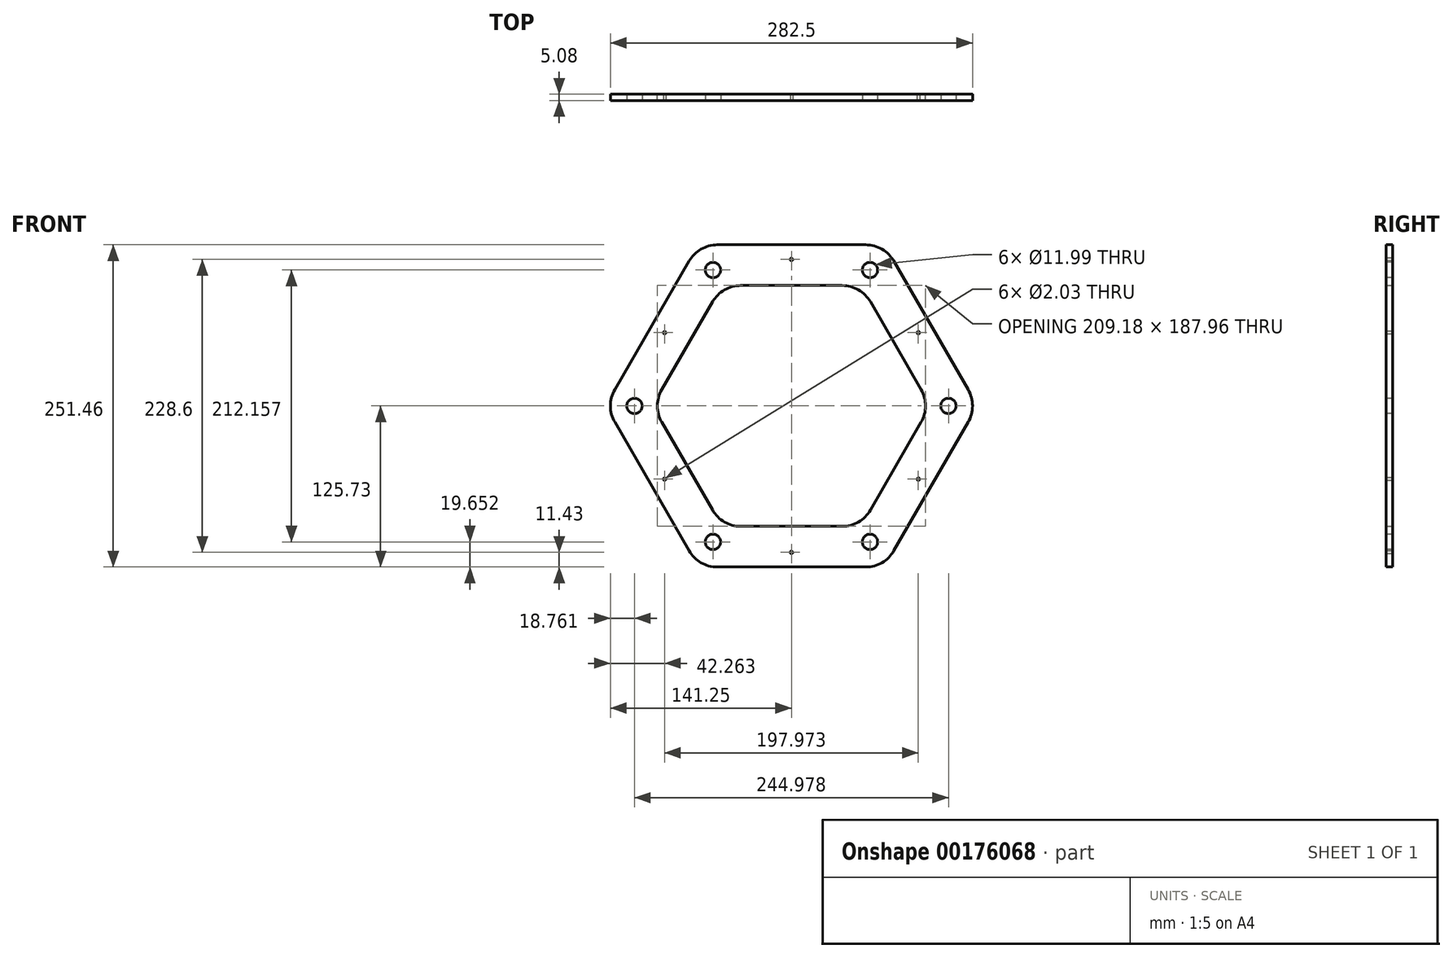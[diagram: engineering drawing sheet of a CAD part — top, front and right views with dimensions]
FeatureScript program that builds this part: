
annotation { "Feature Type Name" : "Feature", "Feature Type Description" : "" }
export const myFeature = defineFeature(function(context is Context, id is Id, definition is map)
    precondition{}
    {
        {
            var Q0;
            Q0=qCreatedBy(makeId("Front.planeOp"),FACE);
            var sketch = newSketch(context, id + "F0", { "sketchPlane" : qUnion([Q0])});
            skCircle(sketch, "E0.cCircle", {"center": v(0, 0) * mm, "radius": 93.98 * mm, "construction": true});
            skLineSegment(sketch, "E0.0", {"start": v(61.6, 81.28) * mm, "end": v(101.19, 12.7) * mm});
            skLineSegment(sketch, "E0.1", {"start": v(101.19, -12.7) * mm, "end": v(61.6, -81.28) * mm});
            skLineSegment(sketch, "E0.2", {"start": v(39.6, -93.98) * mm, "end": v(-39.6, -93.98) * mm});
            skLineSegment(sketch, "E0.3", {"start": v(-61.6, -81.28) * mm, "end": v(-101.19, -12.7) * mm});
            skLineSegment(sketch, "E0.4", {"start": v(-101.19, 12.7) * mm, "end": v(-61.6, 81.28) * mm});
            skLineSegment(sketch, "E0.5", {"start": v(-39.6, 93.98) * mm, "end": v(39.6, 93.98) * mm});
            skPoint(sketch, "E0.0.midPoint", {"position": v(81.39, 46.99) * mm});
            skCircle(sketch, "E1.cCircle", {"center": v(0, 0) * mm, "radius": 125.73 * mm, "construction": true});
            skLineSegment(sketch, "E1.0", {"start": v(-57.93, 125.73) * mm, "end": v(57.93, 125.73) * mm});
            skLineSegment(sketch, "E1.1", {"start": v(79.92, 113.03) * mm, "end": v(137.85, 12.7) * mm});
            skLineSegment(sketch, "E1.2", {"start": v(137.85, -12.7) * mm, "end": v(79.92, -113.03) * mm});
            skLineSegment(sketch, "E1.3", {"start": v(57.93, -125.73) * mm, "end": v(-57.93, -125.73) * mm});
            skLineSegment(sketch, "E1.4", {"start": v(-79.92, -113.03) * mm, "end": v(-137.85, -12.7) * mm});
            skLineSegment(sketch, "E1.5", {"start": v(-137.85, 12.7) * mm, "end": v(-79.92, 113.03) * mm});
            skPoint(sketch, "E1.0.midPoint", {"position": v(0, 125.73) * mm});
            skPoint(sketch, "E2.visualSharp", {"position": v(-72.6, 125.73) * mm});
            skArc(sketch, "E2.filletArc", {"start": v(-57.93, 125.73) * mm, "mid": v(-70.63, 122.33) * mm, "end": v(-79.92, 113.03) * mm});
            skPoint(sketch, "E3.visualSharp", {"position": v(72.6, 125.73) * mm});
            skArc(sketch, "E3.filletArc", {"start": v(79.92, 113.03) * mm, "mid": v(70.63, 122.33) * mm, "end": v(57.93, 125.73) * mm});
            skPoint(sketch, "E4.visualSharp", {"position": v(145.18, 0) * mm});
            skArc(sketch, "E4.filletArc", {"start": v(137.85, -12.7) * mm, "mid": v(141.25, 0) * mm, "end": v(137.85, 12.7) * mm});
            skPoint(sketch, "E5.visualSharp", {"position": v(72.6, -125.73) * mm});
            skArc(sketch, "E5.filletArc", {"start": v(57.93, -125.73) * mm, "mid": v(70.63, -122.33) * mm, "end": v(79.92, -113.03) * mm});
            skPoint(sketch, "E6.visualSharp", {"position": v(-72.6, -125.73) * mm});
            skArc(sketch, "E6.filletArc", {"start": v(-79.92, -113.03) * mm, "mid": v(-70.63, -122.33) * mm, "end": v(-57.93, -125.73) * mm});
            skPoint(sketch, "E7.visualSharp", {"position": v(-145.18, 0) * mm});
            skArc(sketch, "E7.filletArc", {"start": v(-137.85, 12.7) * mm, "mid": v(-141.25, 0) * mm, "end": v(-137.85, -12.7) * mm});
            skPoint(sketch, "E8.visualSharp", {"position": v(-54.26, 93.98) * mm});
            skArc(sketch, "E8.filletArc", {"start": v(-39.6, 93.98) * mm, "mid": v(-52.3, 90.58) * mm, "end": v(-61.6, 81.28) * mm});
            skPoint(sketch, "E9.visualSharp", {"position": v(54.26, 93.98) * mm});
            skArc(sketch, "E9.filletArc", {"start": v(61.6, 81.28) * mm, "mid": v(52.3, 90.58) * mm, "end": v(39.6, 93.98) * mm});
            skPoint(sketch, "E10.visualSharp", {"position": v(108.52, 0) * mm});
            skArc(sketch, "E10.filletArc", {"start": v(101.19, -12.7) * mm, "mid": v(104.59, 0) * mm, "end": v(101.19, 12.7) * mm});
            skPoint(sketch, "E11.visualSharp", {"position": v(54.26, -93.98) * mm});
            skArc(sketch, "E11.filletArc", {"start": v(39.6, -93.98) * mm, "mid": v(52.3, -90.58) * mm, "end": v(61.6, -81.28) * mm});
            skPoint(sketch, "E12.visualSharp", {"position": v(-54.26, -93.98) * mm});
            skArc(sketch, "E12.filletArc", {"start": v(-61.6, -81.28) * mm, "mid": v(-52.3, -90.58) * mm, "end": v(-39.6, -93.98) * mm});
            skPoint(sketch, "E13.visualSharp", {"position": v(-108.52, 0) * mm});
            skArc(sketch, "E13.filletArc", {"start": v(-101.19, 12.7) * mm, "mid": v(-104.59, 0) * mm, "end": v(-101.19, -12.7) * mm});
            skSolve(sketch);
        }
        {
            var Q0;
            Q0 = qSketchRegion(id + "F0", true);
            extrude(context, id + "F1", {"entities" : qUnion([Q0]), "depth" : 5.08 * mm});
        }
        {
            var Q0;
            Q0=makeQuery(id+"F1.opExtrude","CAP_FACE",FACE,{"disambiguationData":[OSD([sQuery(id+"F0.wireOp",EDGE,"E0.0"),sQuery(id+"F0.wireOp",EDGE,"E0.1"),sQuery(id+"F0.wireOp",EDGE,"E0.2"),sQuery(id+"F0.wireOp",EDGE,"E0.3"),sQuery(id+"F0.wireOp",EDGE,"E0.4"),sQuery(id+"F0.wireOp",EDGE,"E0.5"),sQuery(id+"F0.wireOp",EDGE,"E1.0"),sQuery(id+"F0.wireOp",EDGE,"E1.1"),sQuery(id+"F0.wireOp",EDGE,"E1.2"),sQuery(id+"F0.wireOp",EDGE,"E1.3"),sQuery(id+"F0.wireOp",EDGE,"E1.4"),sQuery(id+"F0.wireOp",EDGE,"E1.5"),sQuery(id+"F0.wireOp",EDGE,"E2.filletArc"),sQuery(id+"F0.wireOp",EDGE,"E3.filletArc"),sQuery(id+"F0.wireOp",EDGE,"E4.filletArc"),sQuery(id+"F0.wireOp",EDGE,"E5.filletArc"),sQuery(id+"F0.wireOp",EDGE,"E6.filletArc"),sQuery(id+"F0.wireOp",EDGE,"E7.filletArc"),sQuery(id+"F0.wireOp",EDGE,"E8.filletArc"),sQuery(id+"F0.wireOp",EDGE,"E9.filletArc"),sQuery(id+"F0.wireOp",EDGE,"E10.filletArc"),sQuery(id+"F0.wireOp",EDGE,"E11.filletArc"),sQuery(id+"F0.wireOp",EDGE,"E12.filletArc"),sQuery(id+"F0.wireOp",EDGE,"E13.filletArc")])],"isStart":false});
            var sketch = newSketch(context, id + "F2", { "sketchPlane" : qUnion([Q0])});
            skCircle(sketch, "E14", {"center": v(-61.24, 106.08) * mm, "radius": 6 * mm});
            skLineSegment(sketch, "E15", {"start": v(-72.6, 125.73) * mm, "end": v(-54.26, 93.98) * mm, "construction": true});
            skCircle(sketch, "E16.1.0", {"center": v(-122.49, 0) * mm, "radius": 6 * mm});
            skCircle(sketch, "E16.2.0", {"center": v(-61.24, -106.08) * mm, "radius": 6 * mm});
            skCircle(sketch, "E16.3.0", {"center": v(61.24, -106.08) * mm, "radius": 6 * mm});
            skCircle(sketch, "E16.4.0", {"center": v(122.49, 0) * mm, "radius": 6 * mm});
            skCircle(sketch, "E16.5.0", {"center": v(61.24, 106.08) * mm, "radius": 6 * mm});
            skPoint(sketch, "E16.center", {"position": v(0, 0) * mm});
            skSolve(sketch);
        }
        {
            var Q0;
            Q0 = qSketchRegion(id + "F2", true);
            var Q1;
            Q1=makeQuery(id+"F1.opExtrude","CAP_FACE",FACE,{"disambiguationData":[OSD([sQuery(id+"F0.wireOp",EDGE,"E0.0"),sQuery(id+"F0.wireOp",EDGE,"E0.1"),sQuery(id+"F0.wireOp",EDGE,"E0.2"),sQuery(id+"F0.wireOp",EDGE,"E0.3"),sQuery(id+"F0.wireOp",EDGE,"E0.4"),sQuery(id+"F0.wireOp",EDGE,"E0.5"),sQuery(id+"F0.wireOp",EDGE,"E1.0"),sQuery(id+"F0.wireOp",EDGE,"E1.1"),sQuery(id+"F0.wireOp",EDGE,"E1.2"),sQuery(id+"F0.wireOp",EDGE,"E1.3"),sQuery(id+"F0.wireOp",EDGE,"E1.4"),sQuery(id+"F0.wireOp",EDGE,"E1.5"),sQuery(id+"F0.wireOp",EDGE,"E2.filletArc"),sQuery(id+"F0.wireOp",EDGE,"E3.filletArc"),sQuery(id+"F0.wireOp",EDGE,"E4.filletArc"),sQuery(id+"F0.wireOp",EDGE,"E5.filletArc"),sQuery(id+"F0.wireOp",EDGE,"E6.filletArc"),sQuery(id+"F0.wireOp",EDGE,"E7.filletArc"),sQuery(id+"F0.wireOp",EDGE,"E8.filletArc"),sQuery(id+"F0.wireOp",EDGE,"E9.filletArc"),sQuery(id+"F0.wireOp",EDGE,"E10.filletArc"),sQuery(id+"F0.wireOp",EDGE,"E11.filletArc"),sQuery(id+"F0.wireOp",EDGE,"E12.filletArc"),sQuery(id+"F0.wireOp",EDGE,"E13.filletArc")])],"isStart":true});
            extrude(context, id + "F3", {"entities" : qUnion([Q0]), "operationType" : NewBodyOperationType.REMOVE, "endBound" : BoundingType.UP_TO_SURFACE, "oppositeDirection" : true, "endBoundEntityFace" : qUnion([Q1]), "depth" : 25.4 * mm});
        }
        {
            var Q0;
            Q0=makeQuery(id+"F1.opExtrude","CAP_FACE",FACE,{"disambiguationData":[OSD([sQuery(id+"F0.wireOp",EDGE,"E0.0"),sQuery(id+"F0.wireOp",EDGE,"E0.1"),sQuery(id+"F0.wireOp",EDGE,"E0.2"),sQuery(id+"F0.wireOp",EDGE,"E0.3"),sQuery(id+"F0.wireOp",EDGE,"E0.4"),sQuery(id+"F0.wireOp",EDGE,"E0.5"),sQuery(id+"F0.wireOp",EDGE,"E1.0"),sQuery(id+"F0.wireOp",EDGE,"E1.1"),sQuery(id+"F0.wireOp",EDGE,"E1.2"),sQuery(id+"F0.wireOp",EDGE,"E1.3"),sQuery(id+"F0.wireOp",EDGE,"E1.4"),sQuery(id+"F0.wireOp",EDGE,"E1.5"),sQuery(id+"F0.wireOp",EDGE,"E2.filletArc"),sQuery(id+"F0.wireOp",EDGE,"E3.filletArc"),sQuery(id+"F0.wireOp",EDGE,"E4.filletArc"),sQuery(id+"F0.wireOp",EDGE,"E5.filletArc"),sQuery(id+"F0.wireOp",EDGE,"E6.filletArc"),sQuery(id+"F0.wireOp",EDGE,"E7.filletArc"),sQuery(id+"F0.wireOp",EDGE,"E8.filletArc"),sQuery(id+"F0.wireOp",EDGE,"E9.filletArc"),sQuery(id+"F0.wireOp",EDGE,"E10.filletArc"),sQuery(id+"F0.wireOp",EDGE,"E11.filletArc"),sQuery(id+"F0.wireOp",EDGE,"E12.filletArc"),sQuery(id+"F0.wireOp",EDGE,"E13.filletArc")])],"isStart":false});
            var sketch = newSketch(context, id + "F4", { "sketchPlane" : qUnion([Q0])});
            skCircle(sketch, "E17", {"center": v(0, 114.3) * mm, "radius": 1.02 * mm});
            skCircle(sketch, "E18.1.0", {"center": v(-98.99, 57.15) * mm, "radius": 1.02 * mm});
            skCircle(sketch, "E18.2.0", {"center": v(-98.99, -57.15) * mm, "radius": 1.02 * mm});
            skCircle(sketch, "E18.3.0", {"center": v(0, -114.3) * mm, "radius": 1.02 * mm});
            skCircle(sketch, "E18.4.0", {"center": v(98.99, -57.15) * mm, "radius": 1.02 * mm});
            skCircle(sketch, "E18.5.0", {"center": v(98.99, 57.15) * mm, "radius": 1.02 * mm});
            skPoint(sketch, "E18.center", {"position": v(0, 0) * mm});
            skSolve(sketch);
        }
        {
            var Q0;
            Q0 = qSketchRegion(id + "F4", true);
            extrude(context, id + "F5", {"entities" : qUnion([Q0]), "operationType" : NewBodyOperationType.REMOVE, "endBound" : BoundingType.THROUGH_ALL, "oppositeDirection" : true, "depth" : 25.4 * mm});
        }
    });
